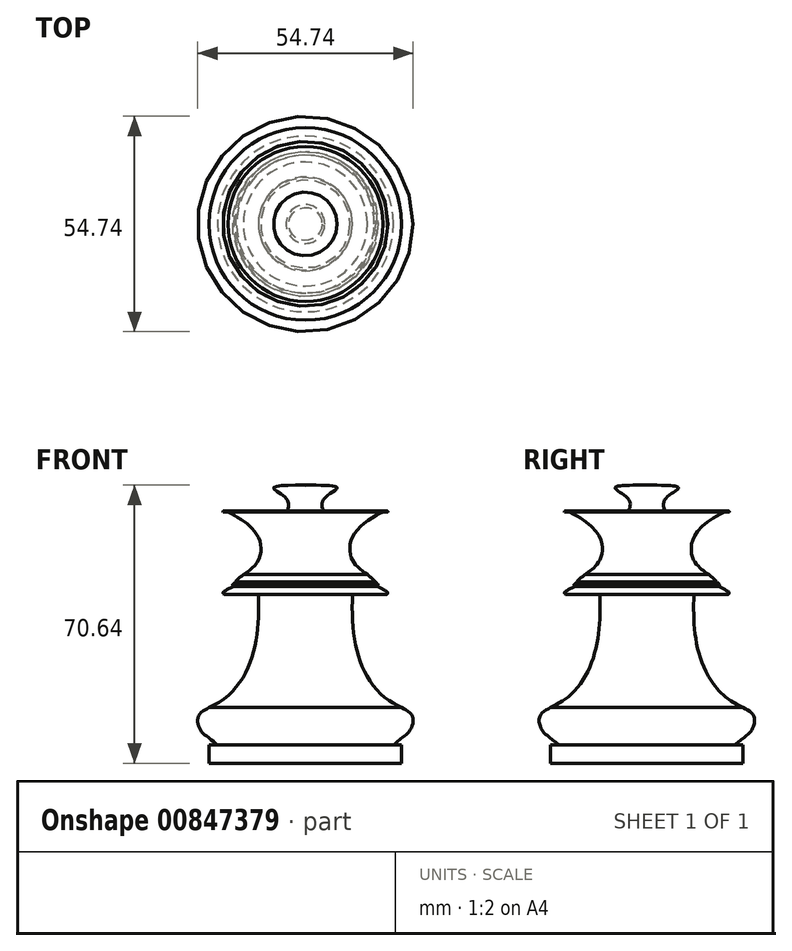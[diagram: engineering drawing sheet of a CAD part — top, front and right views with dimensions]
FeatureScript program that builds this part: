
annotation { "Feature Type Name" : "Feature", "Feature Type Description" : "" }
export const myFeature = defineFeature(function(context is Context, id is Id, definition is map)
    precondition{}
    {
        {
            var Q0;
            Q0=qCreatedBy(makeId("Front.planeOp"),FACE);
            var sketch = newSketch(context, id + "F0", { "sketchPlane" : qUnion([Q0])});
            skLineSegment(sketch, "E0", {"start": v(0, 52.54) * mm, "end": v(0, -49.1) * mm});
            skLineSegment(sketch, "E1", {"start": v(0, -42.87) * mm, "end": v(24.46, -42.87) * mm});
            skLineSegment(sketch, "E2", {"start": v(24.46, -42.87) * mm, "end": v(24.46, -38.25) * mm});
            skLineSegment(sketch, "E3", {"start": v(24.46, -38.25) * mm, "end": v(4.46, -38.25) * mm});
            skPoint(sketch, "E4.4.internal.orphan", {"position": v(24.46, -28.73) * mm});
            skFitSpline(sketch, "E5", {"points": [v(22.32, -38.25) * mm, v(24.46, -36.46) * mm, v(26.54, -34.55) * mm, v(27.22, -31.01) * mm, v(24.46, -28.73) * mm], "startDerivative": vector(9.03, 7.99) * mm, "endDerivative": vector(-13.43, 6.97) * mm});
            skFitSpline(sketch, "E6", {"points": [v(24.46, -28.73) * mm, v(20.1, -26.15) * mm, v(15.98, -21.29) * mm, v(13.47, -15.62) * mm, v(12.1, -8.58) * mm, v(11.93, 0) * mm], "startDerivative": vector(-25.43, 12.5) * mm, "endDerivative": vector(0.6, 38.48) * mm});
            skLineSegment(sketch, "E7", {"start": v(11.93, 0) * mm, "end": v(20.64, 0) * mm});
            skFitSpline(sketch, "E8", {"points": [v(20.64, 0) * mm, v(20.84, 0.2) * mm, v(20.87, 0.56) * mm, v(20.64, 0.8) * mm, v(18.28, 2) * mm], "startDerivative": vector(1.46, 1.08) * mm, "endDerivative": vector(-6.07, 2.93) * mm});
            skFitSpline(sketch, "E9", {"points": [v(18.28, 2) * mm, v(17.46, 2.42) * mm], "startDerivative": vector(-0.82, 0.41) * mm, "endDerivative": vector(-0.82, 0.41) * mm});
            skFitSpline(sketch, "E10", {"points": [v(17.46, 2.42) * mm, v(18.5, 2.42) * mm, v(18.28, 2.73) * mm, v(17.46, 3.23) * mm], "startDerivative": vector(3.72, -0.43) * mm, "endDerivative": vector(-2.39, 1.24) * mm});
            skFitSpline(sketch, "E11", {"points": [v(17.46, 3.23) * mm, v(17.76, 3.23) * mm, v(15.74, 5.06) * mm], "startDerivative": vector(1.68, -0.3) * mm, "endDerivative": vector(-4.14, 3.36) * mm});
            skFitSpline(sketch, "E12", {"points": [v(15.74, 5.06) * mm, v(11.79, 9.04) * mm, v(13.16, 16.37) * mm, v(20.87, 21.18) * mm, v(20.87, 20.72) * mm], "startDerivative": vector(-17.64, 12.47) * mm, "endDerivative": vector(-2.7, -7.67) * mm});
            skLineSegment(sketch, "E13", {"start": v(20.94, 20.91) * mm, "end": v(15.91, 20.91) * mm});
            skLineSegment(sketch, "E14", {"start": v(15.91, 20.91) * mm, "end": v(4.92, 20.91) * mm});
            skFitSpline(sketch, "E15", {"points": [v(4.92, 20.91) * mm, v(4.3, 22.15) * mm, v(4.92, 24.55) * mm, v(8.07, 27.07) * mm, v(0, 27.76) * mm], "startDerivative": vector(-4.85, 7.12) * mm, "endDerivative": vector(-32.68, -0.28) * mm});
            skSolve(sketch);
        }
        {
            var Q0;
            Q0 = qSketchRegion(id + "F0", true);
            var Q1;
            Q1=sQuery(id+"F0.wireOp",EDGE,"E0");
            revolve(context, id + "F1", {"surfaceOperationType" : NewSurfaceOperationType.NEW, "entities" : qUnion([Q0]), "axis" : qUnion([Q1]), "revolveType" : RevolveType.FULL});
        }
    });
